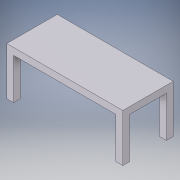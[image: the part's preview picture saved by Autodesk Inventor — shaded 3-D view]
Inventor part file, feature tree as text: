
AUTODESK INVENTOR PART (.ipt)
format: ipt  version: 2017 (Build 210142000, 142)  size: 122,368 bytes
history: native  units: in
note: dims shown in document units (in); Inventor stores cm internally (conversion verified against a paired STEP export)
features: sketch x4, extrude x3
ambient origin geometry x8: Origin, YZ Plane, XZ Plane, XY Plane, X Axis, Y Axis, Z Axis, Center Point
bodies: Solid1 (feature_tree)
feature tree (7):
  sketch  "Sketch1"  dims[d0=27.5591in d1=66.9291in]
  extrude  "Extrusion1"  Depth=66.9291in
  extrude  "Extrusion2"  Depth=3.937in
  extrude  "Extrusion3"  Depth=3.937in
  sketch  "Sketch2"  dims[d2=29.1339in d3=0.0in d4=3.937in]
  sketch  "Sketch3"  dims[d5=3.937in d6=3.937in]
  sketch  "Sketch4"  dims[d7=29.1339in d8=0.0in d9=3.937in d10=3.937in d11=3.937in d12=157.4803in d13=0.0in]
